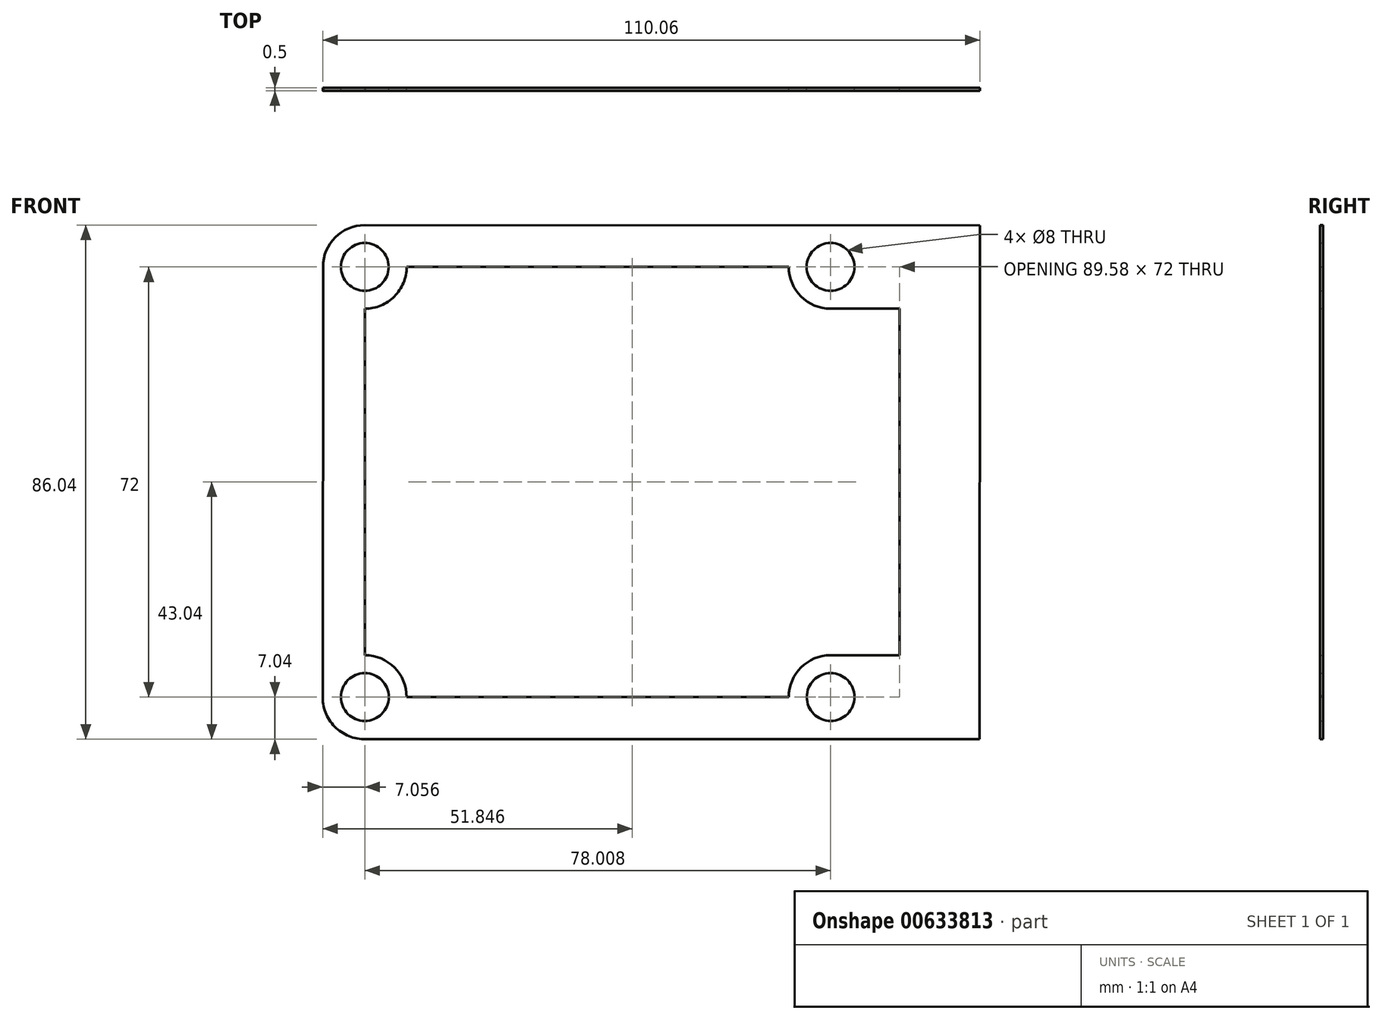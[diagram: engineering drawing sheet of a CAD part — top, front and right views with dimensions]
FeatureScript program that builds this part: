
annotation { "Feature Type Name" : "Feature", "Feature Type Description" : "" }
export const myFeature = defineFeature(function(context is Context, id is Id, definition is map)
    precondition{}
    {
        {
            var Q0;
            Q0=qCreatedBy(makeId("Front.planeOp"),FACE);
            var sketch = newSketch(context, id + "F0", { "sketchPlane" : qUnion([Q0])});
            skPoint(sketch, "E0.middle", {"position": v(0, 0) * mm});
            skCircle(sketch, "E1", {"center": v(-39, 36) * mm, "radius": 4 * mm});
            skCircle(sketch, "E2", {"center": v(39, 36) * mm, "radius": 4 * mm});
            skCircle(sketch, "E3", {"center": v(-39, -36) * mm, "radius": 4 * mm});
            skCircle(sketch, "E4", {"center": v(39, -36) * mm, "radius": 4 * mm});
            skLineSegment(sketch, "E5.bottom", {"start": v(-32, 36) * mm, "end": v(32, 36) * mm});
            skLineSegment(sketch, "E5.top", {"start": v(-32, -36) * mm, "end": v(32, -36) * mm});
            skLineSegment(sketch, "E6.left", {"start": v(-39, 29) * mm, "end": v(-39, -29) * mm});
            skLineSegment(sketch, "E7.right", {"start": v(64, 42.96) * mm, "end": v(63.95, -43.04) * mm});
            skLineSegment(sketch, "E8.bottom", {"start": v(39, 29) * mm, "end": v(50.58, 29) * mm});
            skLineSegment(sketch, "E8.top", {"start": v(39, -29) * mm, "end": v(50.58, -29) * mm});
            skLineSegment(sketch, "E8.right", {"start": v(50.58, 29) * mm, "end": v(50.58, -29) * mm});
            skArc(sketch, "E9", {"start": v(-39, 29) * mm, "mid": v(-34.05, 31.05) * mm, "end": v(-32, 36) * mm});
            skArc(sketch, "E10", {"start": v(-39, 43) * mm, "mid": v(-43.95, 40.95) * mm, "end": v(-46, 36) * mm});
            skArc(sketch, "E11", {"start": v(32, 36) * mm, "mid": v(34.05, 31.05) * mm, "end": v(39, 29) * mm});
            skArc(sketch, "E12", {"start": v(-32, -36) * mm, "mid": v(-34.05, -31.05) * mm, "end": v(-39, -29) * mm});
            skArc(sketch, "E13", {"start": v(-46.05, -35.72) * mm, "mid": v(-44.05, -40.95) * mm, "end": v(-38.86, -43.04) * mm});
            skArc(sketch, "E14", {"start": v(39, -29) * mm, "mid": v(34.05, -31.05) * mm, "end": v(32, -36) * mm});
            skLineSegment(sketch, "E15", {"start": v(-39, 43) * mm, "end": v(64, 42.96) * mm});
            skLineSegment(sketch, "E16", {"start": v(-46, 36) * mm, "end": v(-46.05, -35.72) * mm});
            skLineSegment(sketch, "E17", {"start": v(-38.86, -43.04) * mm, "end": v(63.95, -43.04) * mm});
            skSolve(sketch);
        }
        {
            var Q0;
            Q0 = qSketchRegion(id + "F0", true);
            extrude(context, id + "F1", {"entities" : qUnion([Q0]), "depth" : 0.5 * mm, "offsetDistance" : 25 * mm});
        }
    });
